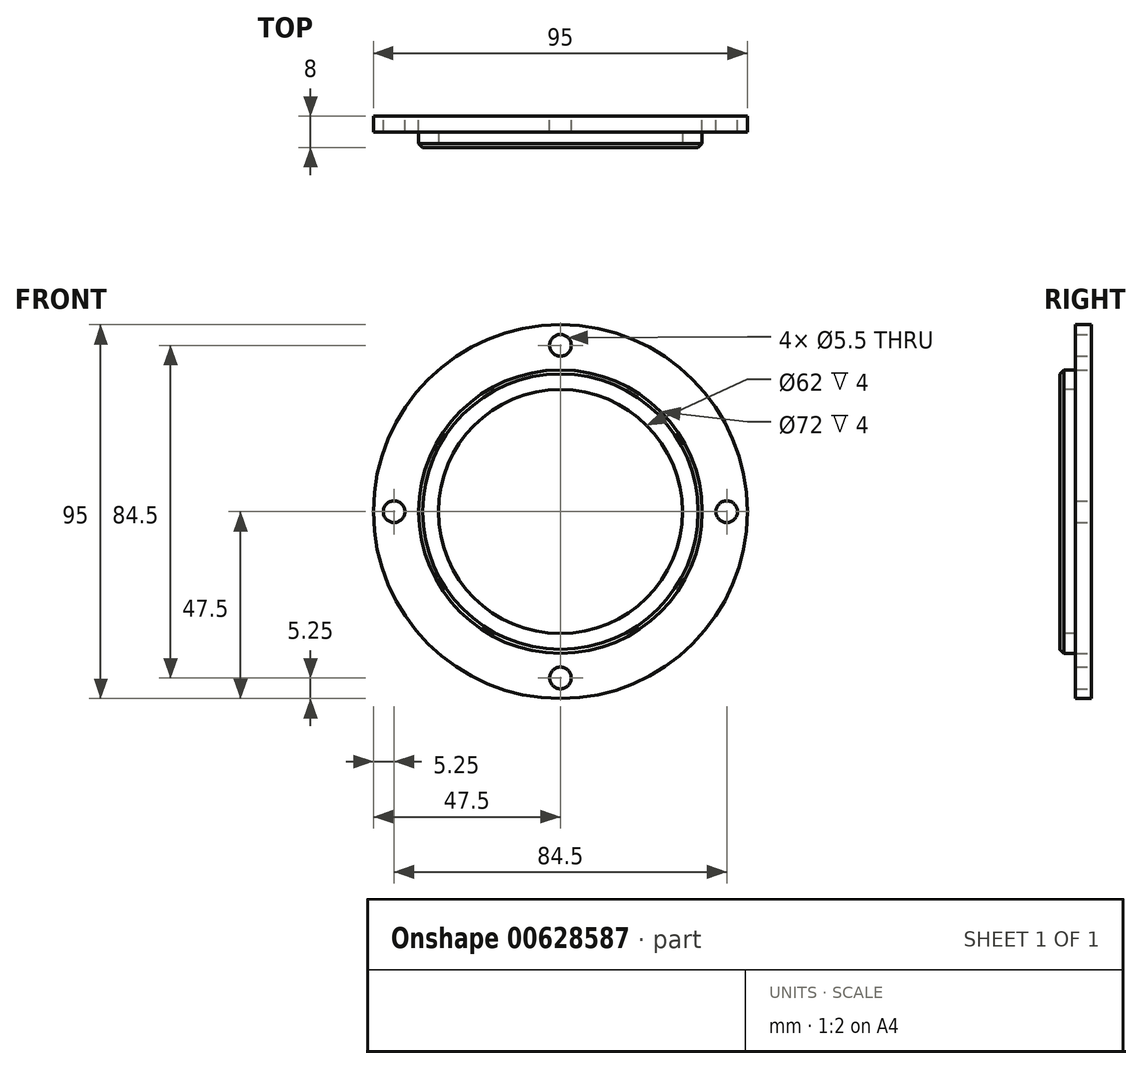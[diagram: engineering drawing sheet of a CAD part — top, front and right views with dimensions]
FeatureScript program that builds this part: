
annotation { "Feature Type Name" : "Feature", "Feature Type Description" : "" }
export const myFeature = defineFeature(function(context is Context, id is Id, definition is map)
    precondition{}
    {
        {
            var Q0;
            Q0=qCreatedBy(makeId("Front.planeOp"),FACE);
            var sketch = newSketch(context, id + "F0", { "sketchPlane" : qUnion([Q0])});
            skCircle(sketch, "E0", {"center": v(0, 0) * mm, "radius": 47.5 * mm});
            skCircle(sketch, "E1", {"center": v(0, 0) * mm, "radius": 42.25 * mm, "construction": true});
            skCircle(sketch, "E2", {"center": v(0, 0) * mm, "radius": 36 * mm});
            skCircle(sketch, "E3", {"center": v(0, 0) * mm, "radius": 31 * mm});
            skLineSegment(sketch, "E4", {"start": v(-51.6, 0) * mm, "end": v(61.65, 0) * mm, "construction": true});
            skLineSegment(sketch, "E5", {"start": v(0, 56.4) * mm, "end": v(0, -63.39) * mm, "construction": true});
            skCircle(sketch, "E6", {"center": v(42.25, 0) * mm, "radius": 2.75 * mm});
            skCircle(sketch, "E7.MirrorC", {"center": v(-42.25, 0) * mm, "radius": 2.75 * mm});
            skCircle(sketch, "E8", {"center": v(0, 42.25) * mm, "radius": 2.75 * mm});
            skCircle(sketch, "E9.MirrorC", {"center": v(0, -42.25) * mm, "radius": 2.75 * mm});
            skSolve(sketch);
        }
        {
            var Q0;
            Q0 = qSketchRegion(id + "F0", true);
            extrude(context, id + "F1", {"entities" : qUnion([Q0]), "depth" : 4 * mm, "offsetDistance" : 25 * mm});
        }
        {
            var Q0;
            Q0=makeQuery(id+"F1.opExtrude","CAP_FACE",FACE,{"disambiguationData":[OSD([sQuery(id+"F0.wireOp",EDGE,"E0"),sQuery(id+"F0.wireOp",EDGE,"E2"),sQuery(id+"F0.wireOp",EDGE,"E6"),sQuery(id+"F0.wireOp",EDGE,"E7.MirrorC"),sQuery(id+"F0.wireOp",EDGE,"E8"),sQuery(id+"F0.wireOp",EDGE,"E9.MirrorC")])],"isStart":false});
            var sketch = newSketch(context, id + "F2", { "sketchPlane" : qUnion([Q0])});
            skCircle(sketch, "E10.0", {"center": v(0, 0) * mm, "radius": 36 * mm});
            skSolve(sketch);
        }
        {
            var Q0;
            Q0 = qSketchRegion(id + "F2", true);
            extrude(context, id + "F3", {"entities" : qUnion([Q0]), "depth" : 4 * mm, "offsetDistance" : 25 * mm});
        }
        {
            var Q0;
            Q0=makeQuery(id+"F3.opExtrude","CAP_FACE",FACE,{"disambiguationData":[OSD([sQuery(id+"F2.wireOp",EDGE,"E10.0")])],"isStart":false});
            var sketch = newSketch(context, id + "F4", { "sketchPlane" : qUnion([Q0])});
            skCircle(sketch, "E11", {"center": v(0, 0) * mm, "radius": 31 * mm});
            skSolve(sketch);
        }
        {
            var Q0;
            Q0 = qSketchRegion(id + "F4", true);
            extrude(context, id + "F5", {"entities" : qUnion([Q0]), "operationType" : NewBodyOperationType.REMOVE, "endBound" : BoundingType.UP_TO_NEXT, "oppositeDirection" : true, "depth" : 25 * mm, "offsetDistance" : 25 * mm});
        }
        {
            var Q0;
            Q0=makeQuery(id+"F3.opExtrude","CAP_EDGE",EDGE,{"disambiguationData":[OSD([sQuery(id+"F2.wireOp",EDGE,"E10.0")])],"isStart":false});
            chamfer(context, id + "F6", {"entities" : qUnion([Q0]), "width" : 1 * mm, "tangentPropagation" : true});
        }
    });
